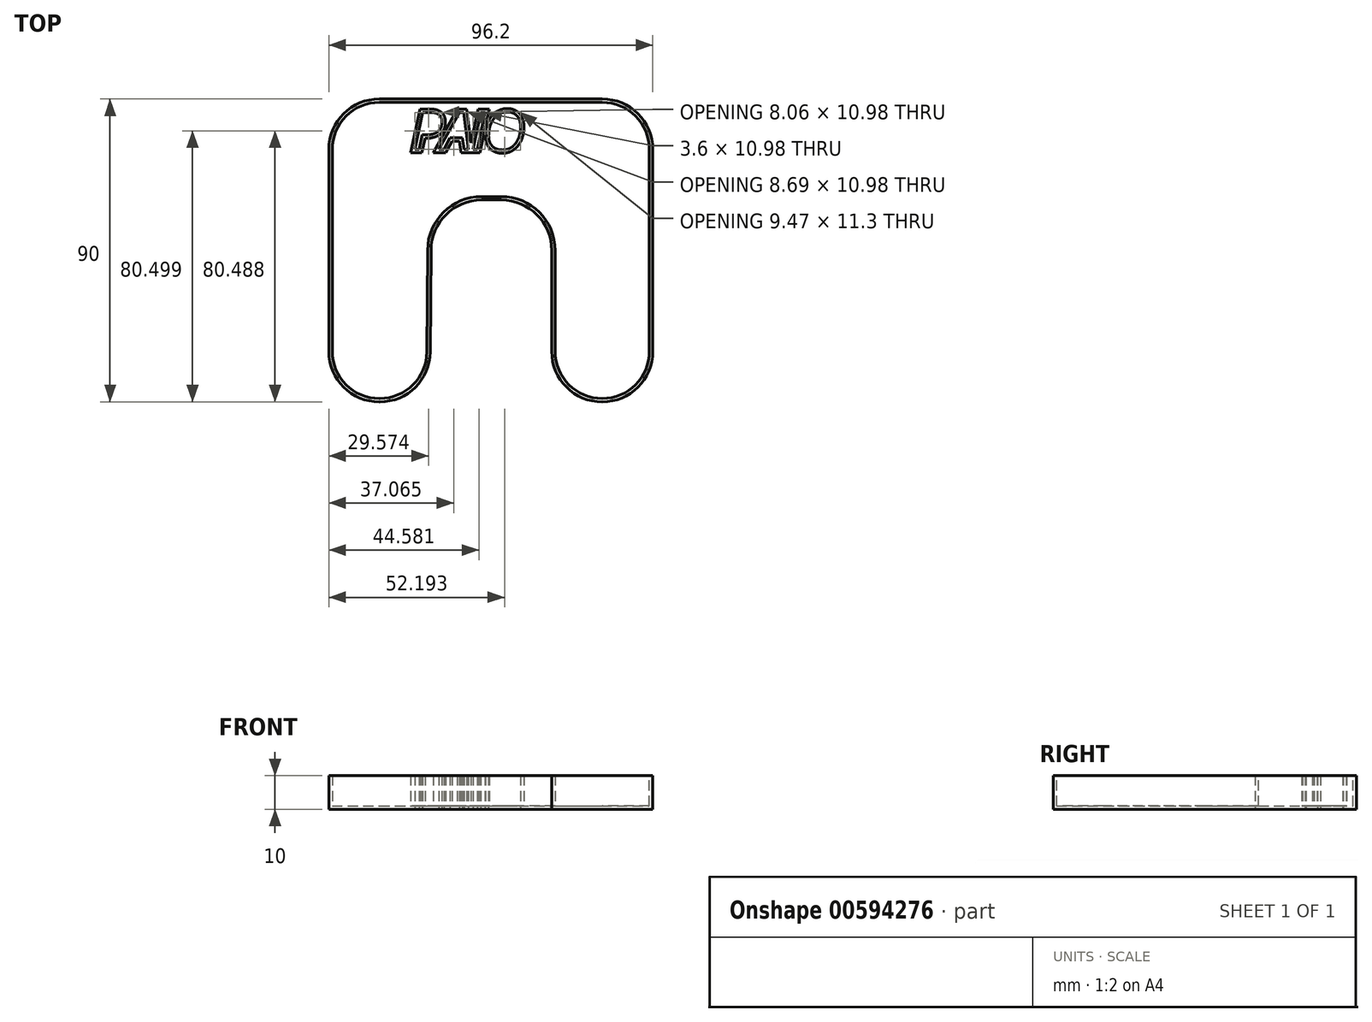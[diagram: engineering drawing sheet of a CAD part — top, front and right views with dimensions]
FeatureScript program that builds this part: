
annotation { "Feature Type Name" : "Feature", "Feature Type Description" : "" }
export const myFeature = defineFeature(function(context is Context, id is Id, definition is map)
    precondition{}
    {
        {
            var Q0;
            Q0=qCreatedBy(makeId("Top.planeOp"),FACE);
            var sketch = newSketch(context, id + "F0", { "sketchPlane" : qUnion([Q0])});
            skLineSegment(sketch, "E0.bottom", {"start": v(15, 0) * mm, "end": v(15.11, 0) * mm});
            skLineSegment(sketch, "E0.top", {"start": v(15, 90) * mm, "end": v(81.2, 90) * mm});
            skLineSegment(sketch, "E0.left", {"start": v(0, 15) * mm, "end": v(0, 75) * mm});
            skLineSegment(sketch, "E0.right", {"start": v(96.2, 15) * mm, "end": v(96.2, 75) * mm});
            skLineSegment(sketch, "E1", {"start": v(30.1, 14.89) * mm, "end": v(30.33, 45.11) * mm});
            skLineSegment(sketch, "E2.trimOffspring", {"start": v(45.33, 60) * mm, "end": v(51.2, 60) * mm});
            skLineSegment(sketch, "E3", {"start": v(66.2, 45) * mm, "end": v(66.2, 15) * mm});
            skPoint(sketch, "E4.visualSharp", {"position": v(0, 90) * mm});
            skArc(sketch, "E4.filletArc", {"start": v(15, 90) * mm, "mid": v(4.4, 85.6) * mm, "end": v(0, 75) * mm});
            skPoint(sketch, "E5.visualSharp", {"position": v(96.2, 90) * mm});
            skArc(sketch, "E5.filletArc", {"start": v(96.2, 75) * mm, "mid": v(91.8, 85.6) * mm, "end": v(81.2, 90) * mm});
            skPoint(sketch, "E6.visualSharp", {"position": v(0, 0) * mm});
            skArc(sketch, "E6.filletArc", {"start": v(0, 15) * mm, "mid": v(4.4, 4.4) * mm, "end": v(15, 0) * mm});
            skPoint(sketch, "E7.newPointA", {"position": v(30, 0) * mm});
            skPoint(sketch, "E7.newPointB", {"position": v(90, 0) * mm});
            skArc(sketch, "E7.filletArc", {"start": v(15.11, 0) * mm, "mid": v(25.68, 4.35) * mm, "end": v(30.1, 14.89) * mm});
            skPoint(sketch, "E8.visualSharp", {"position": v(30.44, 60) * mm});
            skArc(sketch, "E8.filletArc", {"start": v(45.33, 60) * mm, "mid": v(34.77, 55.65) * mm, "end": v(30.33, 45.11) * mm});
            skPoint(sketch, "E9.visualSharp", {"position": v(66.2, 60) * mm});
            skArc(sketch, "E9.filletArc", {"start": v(66.2, 45) * mm, "mid": v(61.8, 55.6) * mm, "end": v(51.2, 60) * mm});
            skLineSegment(sketch, "E10", {"start": v(81.2, 0) * mm, "end": v(81.2, 0) * mm});
            skPoint(sketch, "E11.visualSharp", {"position": v(66.2, 0) * mm});
            skArc(sketch, "E11.filletArc", {"start": v(66.2, 15) * mm, "mid": v(70.6, 4.4) * mm, "end": v(81.2, 0) * mm});
            skPoint(sketch, "E12.visualSharp", {"position": v(96.2, 0) * mm});
            skArc(sketch, "E12.filletArc", {"start": v(81.2, 0) * mm, "mid": v(91.8, 4.4) * mm, "end": v(96.2, 15) * mm});
            skText(sketch, "E13", { "text": "PAIO", "fontName": "OpenSans-Italic.ttf"});
            const initialGuessF0  = {"E13": [0.0249, 0.075, 1, 0, 0.01107]};
            skSetInitialGuess(sketch, initialGuessF0);
            skSolve(sketch);
        }
        {
            var Q0;
            Q0 = qSketchRegion(id + "F0", true);
            extrude(context, id + "F1", {"entities" : qUnion([Q0]), "depth" : 10 * mm, "offsetDistance" : 25 * mm});
        }
        {
            var Q0;
            Q0=makeQuery(id+"F1.opExtrude","CAP_FACE",FACE,{"disambiguationData":[OSD([sQuery(id+"F0.wireOp",EDGE,"E0.bottom"),sQuery(id+"F0.wireOp",EDGE,"E0.top"),sQuery(id+"F0.wireOp",EDGE,"E0.left"),sQuery(id+"F0.wireOp",EDGE,"E0.right"),sQuery(id+"F0.wireOp",EDGE,"E1"),sQuery(id+"F0.wireOp",EDGE,"E2.trimOffspring"),sQuery(id+"F0.wireOp",EDGE,"E3"),sQuery(id+"F0.wireOp",EDGE,"E4.filletArc"),sQuery(id+"F0.wireOp",EDGE,"E5.filletArc"),sQuery(id+"F0.wireOp",EDGE,"E6.filletArc"),sQuery(id+"F0.wireOp",EDGE,"E7.filletArc"),sQuery(id+"F0.wireOp",EDGE,"E8.filletArc"),sQuery(id+"F0.wireOp",EDGE,"E9.filletArc"),sQuery(id+"F0.wireOp",EDGE,"E11.filletArc"),sQuery(id+"F0.wireOp",EDGE,"E12.filletArc")])],"isStart":false});
            shell(context, id + "F2", {"entities" : qUnion([Q0]), "thickness" : 1 * mm});
        }
    });
